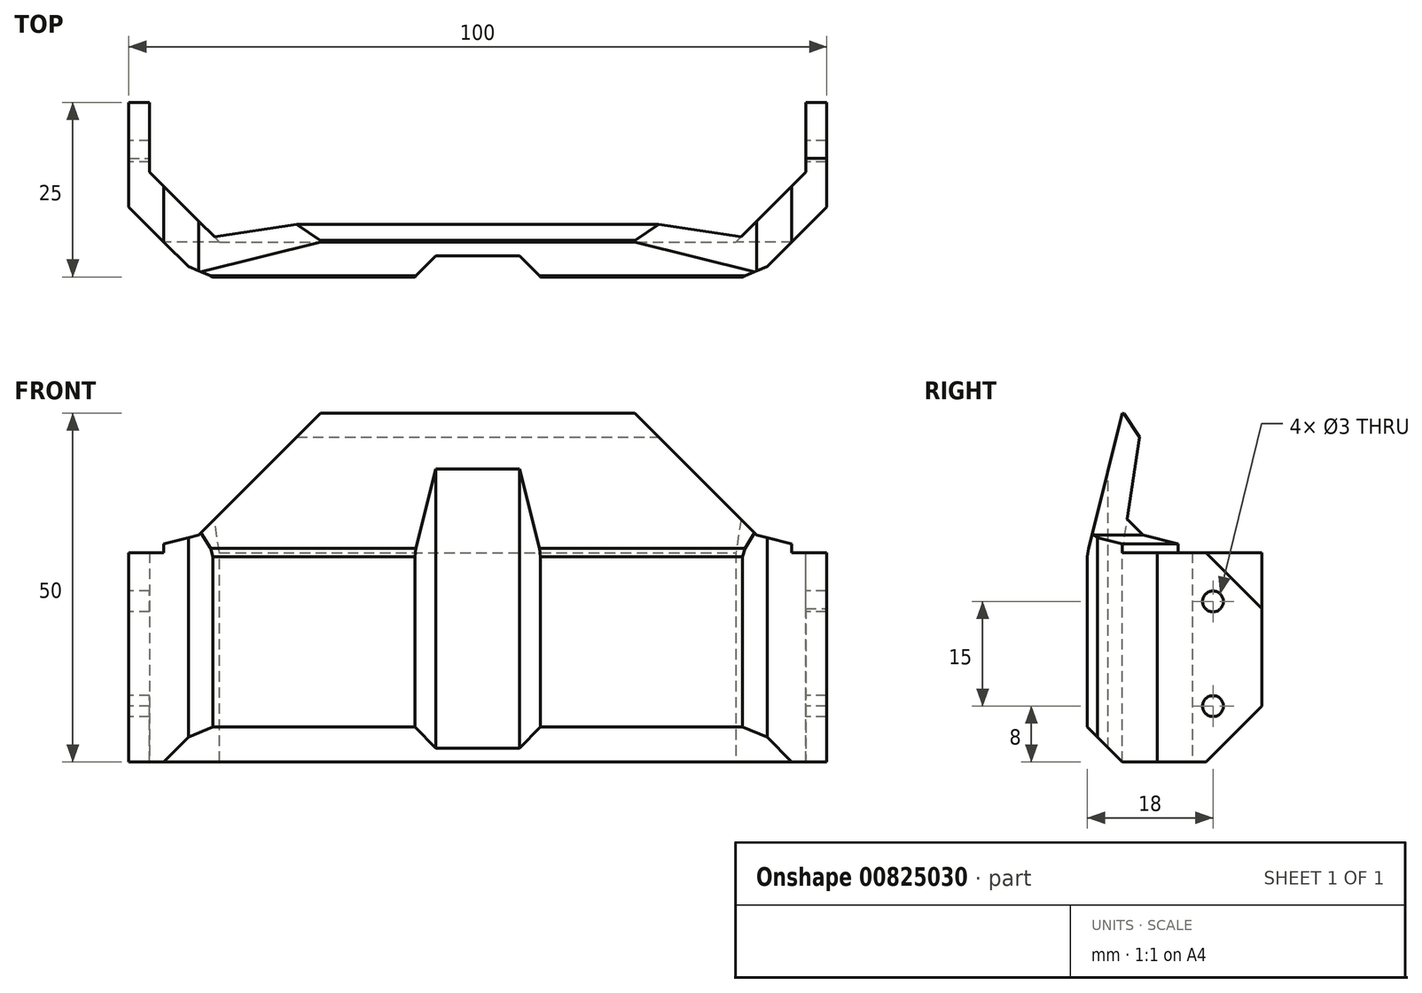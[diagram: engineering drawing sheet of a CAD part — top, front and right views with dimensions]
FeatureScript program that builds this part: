
annotation { "Feature Type Name" : "Feature", "Feature Type Description" : "" }
export const myFeature = defineFeature(function(context is Context, id is Id, definition is map)
    precondition{}
    {
        {
            var Q0;
            Q0=qCreatedBy(makeId("Top.planeOp"),FACE);
            var sketch = newSketch(context, id + "F0", { "sketchPlane" : qUnion([Q0])});
            skLineSegment(sketch, "E0.bottom", {"start": v(-50, 20) * mm, "end": v(50, 20) * mm});
            skLineSegment(sketch, "E0.top", {"start": v(-50, -5) * mm, "end": v(50, -5) * mm});
            skLineSegment(sketch, "E0.left", {"start": v(-50, 20) * mm, "end": v(-50, -5) * mm});
            skLineSegment(sketch, "E0.right", {"start": v(50, 20) * mm, "end": v(50, -5) * mm});
            skLineSegment(sketch, "E1.bottom", {"start": v(-47, 20) * mm, "end": v(47, 20) * mm});
            skLineSegment(sketch, "E1.top", {"start": v(-47, 0) * mm, "end": v(47, 0) * mm});
            skLineSegment(sketch, "E1.left", {"start": v(-47, 20) * mm, "end": v(-47, 0) * mm});
            skLineSegment(sketch, "E1.right", {"start": v(47, 20) * mm, "end": v(47, 0) * mm});
            skSolve(sketch);
        }
        {
            var Q0;
            Q0=makeQuery(id+"F0.imprint","IMPRINT",FACE,{"disambiguationData":[TD([[makeQuery(id+"F0.imprint","IMPRINT",EDGE,{"derivedFrom":sQuery(id+"F0.wireOp",EDGE,"E0.top")}),1.0]])]});
            extrude(context, id + "F1", {"entities" : qUnion([Q0]), "depth" : 30 * mm, "offsetDistance" : 25 * mm});
        }
        {
            var Q0;
            Q0=makeQuery(id+"F1.opExtrude","SWEPT_EDGE",EDGE,{"disambiguationData":[OSD([sQuery(id+"F0.wireOp",EDGE,"E1.top"),sQuery(id+"F0.wireOp",EDGE,"E1.left")])]});
            var Q1;
            Q1=makeQuery(id+"F1.opExtrude","SWEPT_EDGE",EDGE,{"disambiguationData":[OSD([sQuery(id+"F0.wireOp",EDGE,"E1.top"),sQuery(id+"F0.wireOp",EDGE,"E1.right")])]});
            var Q2;
            Q2=makeQuery(id+"F1.opExtrude","SWEPT_EDGE",EDGE,{"disambiguationData":[OSD([sQuery(id+"F0.wireOp",EDGE,"E0.top"),sQuery(id+"F0.wireOp",EDGE,"E0.left")])]});
            var Q3;
            Q3=makeQuery(id+"F1.opExtrude","SWEPT_EDGE",EDGE,{"disambiguationData":[OSD([sQuery(id+"F0.wireOp",EDGE,"E0.top"),sQuery(id+"F0.wireOp",EDGE,"E0.right")])]});
            chamfer(context, id + "F2", {"entities" : qUnion([Q0, Q1, Q2, Q3]), "width" : 10 * mm, "tangentPropagation" : true});
        }
        {
            var Q0;
            Q0=qCreatedBy(makeId("Right.planeOp"),FACE);
            var sketch = newSketch(context, id + "F3", { "sketchPlane" : qUnion([Q0])});
            skLineSegment(sketch, "E2.0.0", {"start": v(5, 30) * mm, "end": v(-5, 30) * mm});
            skLineSegment(sketch, "E2.0.1", {"start": v(5, 30) * mm, "end": v(5, 0) * mm});
            skLineSegment(sketch, "E2.0.2", {"start": v(-5, 0) * mm, "end": v(5, 0) * mm});
            skLineSegment(sketch, "E2.0.3", {"start": v(-5, 0) * mm, "end": v(-5, 30) * mm});
            skLineSegment(sketch, "E3", {"start": v(-5, 30) * mm, "end": v(0, 50) * mm});
            skLineSegment(sketch, "E4", {"start": v(0, 50) * mm, "end": v(2.91, 49.27) * mm});
            skLineSegment(sketch, "E5", {"start": v(2.91, 49.27) * mm, "end": v(0, 30) * mm});
            skSolve(sketch);
        }
        {
            var Q0;
            {var subQ0=sQuery(id+"F3.wireOp",EDGE,"E3");Q0=makeQuery(id+"F3.imprint","IMPRINT",FACE,{"disambiguationData":[TD([[makeQuery(id+"F3.imprint","IMPRINT",EDGE,{"derivedFrom":subQ0}),-1.0]])]});}
            extrude(context, id + "F4", {"entities" : qUnion([Q0]), "operationType" : NewBodyOperationType.ADD, "endBound" : BoundingType.SYMMETRIC, "depth" : 100 * mm, "offsetDistance" : 25 * mm});
        }
        {
            var Q0;
            {var subQ0=sQuery(id+"F0.wireOp",EDGE,"E1.right");var subQ1=sQuery(id+"F0.wireOp",EDGE,"E1.top");var subQ2=sQuery(id+"F0.wireOp",EDGE,"E0.right");var subQ3=sQuery(id+"F0.wireOp",EDGE,"E0.bottom");var subQ4=sQuery(id+"F0.wireOp",EDGE,"E0.top");Q0=makeQuery(id+"F4.boolean.opBoolean","SPLIT",FACE,{"disambiguationData":[TD([makeQuery(id+"F1.opExtrude","SWEPT_FACE",FACE,{"disambiguationData":[OSD([subQ2])]})])],"derivedFrom":makeQuery(id+"F1.opExtrude","CAP_FACE",FACE,{"disambiguationData":[OSD([subQ3,subQ4,sQuery(id+"F0.wireOp",EDGE,"E0.left"),subQ2,subQ1,sQuery(id+"F0.wireOp",EDGE,"E1.left"),subQ0])],"isStart":false})});}
            var Q1;
            {var subQ0=sQuery(id+"F0.wireOp",EDGE,"E1.left");var subQ1=sQuery(id+"F0.wireOp",EDGE,"E1.top");var subQ2=sQuery(id+"F0.wireOp",EDGE,"E0.left");var subQ3=sQuery(id+"F0.wireOp",EDGE,"E0.bottom");var subQ4=sQuery(id+"F0.wireOp",EDGE,"E0.top");Q1=makeQuery(id+"F4.boolean.opBoolean","SPLIT",FACE,{"disambiguationData":[TD([makeQuery(id+"F1.opExtrude","SWEPT_FACE",FACE,{"disambiguationData":[OSD([subQ2])]})])],"derivedFrom":makeQuery(id+"F1.opExtrude","CAP_FACE",FACE,{"disambiguationData":[OSD([subQ3,subQ4,subQ2,sQuery(id+"F0.wireOp",EDGE,"E0.right"),subQ1,subQ0,sQuery(id+"F0.wireOp",EDGE,"E1.right")])],"isStart":false})});}
            extrude(context, id + "F5", {"entities" : qUnion([Q0, Q1]), "operationType" : NewBodyOperationType.ADD, "depth" : 20 * mm, "offsetDistance" : 25 * mm});
        }
        {
            var Q0;
            {var subQ2=sQuery(id+"F3.wireOp",EDGE,"E2.0.0");var subQ3=sQuery(id+"F0.wireOp",EDGE,"E0.top");var subQ4=sQuery(id+"F0.wireOp",EDGE,"E0.right");Q0=makeQuery(id+"F4.boolean.opBoolean","SPLIT",FACE,{"disambiguationData":[TD([makeQuery(id+"F2.opChamfer","BLEND_FACE",FACE,{"disambiguationData":[OSD([subQ3,subQ4])]})])],"derivedFrom":makeQuery(id+"F4.opExtrude","SWEPT_FACE",FACE,{"disambiguationData":[OSD([subQ2])]})});}
            var Q1;
            {var subQ2=sQuery(id+"F3.wireOp",EDGE,"E2.0.0");var subQ3=sQuery(id+"F0.wireOp",EDGE,"E0.left");var subQ4=sQuery(id+"F0.wireOp",EDGE,"E0.top");Q1=makeQuery(id+"F4.boolean.opBoolean","SPLIT",FACE,{"disambiguationData":[TD([makeQuery(id+"F2.opChamfer","BLEND_FACE",FACE,{"disambiguationData":[OSD([subQ4,subQ3])]})])],"derivedFrom":makeQuery(id+"F4.opExtrude","SWEPT_FACE",FACE,{"disambiguationData":[OSD([subQ2])]})});}
            extrude(context, id + "F6", {"entities" : qUnion([Q0, Q1]), "operationType" : NewBodyOperationType.REMOVE, "oppositeDirection" : true, "depth" : 25 * mm, "offsetDistance" : 25 * mm});
        }
        {
            var Q0;
            Q0=makeQuery(id+"F1.opExtrude","SWEPT_FACE",FACE,{"disambiguationData":[OSD([sQuery(id+"F0.wireOp",EDGE,"E0.top")])]});
            var sketch = newSketch(context, id + "F7", { "sketchPlane" : qUnion([Q0])});
            skLineSegment(sketch, "E6.0.0", {"start": v(47.91, 49.27) * mm, "end": v(45, 30) * mm});
            skLineSegment(sketch, "E6.0.1", {"start": v(45, 30) * mm, "end": v(45, 50) * mm});
            skLineSegment(sketch, "E6.0.2", {"start": v(45, 50) * mm, "end": v(40, 30) * mm});
            skLineSegment(sketch, "E6.0.3", {"start": v(40, 30) * mm, "end": v(40, 0) * mm});
            skLineSegment(sketch, "E6.0.4", {"start": v(40, 0) * mm, "end": v(50, 0) * mm});
            skLineSegment(sketch, "E6.0.5", {"start": v(50, 0) * mm, "end": v(50, 50) * mm});
            skLineSegment(sketch, "E6.0.6", {"start": v(50, 50) * mm, "end": v(45, 50) * mm});
            skLineSegment(sketch, "E6.0.7", {"start": v(45, 50) * mm, "end": v(47.91, 49.27) * mm});
            skLineSegment(sketch, "E7", {"start": v(50, 30) * mm, "end": v(45, 30) * mm});
            skLineSegment(sketch, "E8.0.0", {"start": v(40, 30) * mm, "end": v(45, 50) * mm});
            skLineSegment(sketch, "E8.0.1", {"start": v(45, 50) * mm, "end": v(37, 50) * mm});
            skLineSegment(sketch, "E8.0.2", {"start": v(37, 50) * mm, "end": v(-37, 50) * mm});
            skLineSegment(sketch, "E8.0.3", {"start": v(-37, 50) * mm, "end": v(-45, 50) * mm});
            skLineSegment(sketch, "E8.0.4", {"start": v(-45, 50) * mm, "end": v(-40, 30) * mm});
            skLineSegment(sketch, "E8.0.5", {"start": v(-40, 30) * mm, "end": v(40, 30) * mm});
            skLineSegment(sketch, "E9", {"start": v(50, 30) * mm, "end": v(40, 32.5) * mm});
            skLineSegment(sketch, "E10", {"start": v(40, 32.5) * mm, "end": v(22.5, 50) * mm});
            skSolve(sketch);
        }
        {
            var Q0;
            {var subQ1=sQuery(id+"F7.wireOp",EDGE,"E8.0.1");Q0=makeQuery(id+"F7.imprint","IMPRINT",FACE,{"disambiguationData":[TD([[makeQuery(id+"F7.imprint","IMPRINT",EDGE,{"derivedFrom":subQ1}),1.0]])]});}
            var Q1;
            {var subQ1=sQuery(id+"F7.wireOp",EDGE,"E6.0.1");var subQ3=sQuery(id+"F7.wireOp",EDGE,"E9");var subQ4=makeQuery(id+"F7.imprint","INTERSECT",VERTEX,{"derivedFrom":[subQ1,subQ3]});Q1=makeQuery(id+"F7.imprint","IMPRINT",FACE,{"disambiguationData":[TD([[makeQuery(id+"F7.imprint","IMPRINT",EDGE,{"disambiguationData":[TD([[subQ4,-1.0]])],"derivedFrom":subQ3}),-1.0]])]});}
            var Q2;
            {var subQ1=sQuery(id+"F7.wireOp",EDGE,"E6.0.6");Q2=makeQuery(id+"F7.imprint","IMPRINT",FACE,{"disambiguationData":[TD([[makeQuery(id+"F7.imprint","IMPRINT",EDGE,{"derivedFrom":subQ1}),1.0]])]});}
            extrude(context, id + "F8", {"entities" : qUnion([Q0, Q1, Q2]), "operationType" : NewBodyOperationType.REMOVE, "endBound" : BoundingType.THROUGH_ALL, "oppositeDirection" : true, "depth" : 25 * mm, "offsetDistance" : 25 * mm});
        }
        {
            var Q0;
            {var subQ0=sQuery(id+"F3.wireOp",EDGE,"E5");var subQ1=sQuery(id+"F3.wireOp",EDGE,"E2.0.0");var subQ2=makeQuery(id+"F4.opExtrude","SWEPT_FACE",FACE,{"disambiguationData":[OSD([subQ1])]});var subQ3=sQuery(id+"F0.wireOp",EDGE,"E0.right");var subQ4=sQuery(id+"F0.wireOp",EDGE,"E0.top");var subQ5=makeQuery(id+"F4.opExtrude","SWEPT_FACE",FACE,{"disambiguationData":[OSD([subQ0])]});Q0=makeQuery(id+"F6.boolean.opBoolean","COPY",FACE,{"derivedFrom":makeQuery(id+"F6.opExtrude","SWEPT_FACE",FACE,{"disambiguationData":[OSD([subQ1,subQ0]),TDD([makeQuery(id+"F4.boolean.opBoolean","SPLIT",EDGE,{"disambiguationData":[topologyDisambiguationEdgeConnected([subQ2,subQ5]),TD([makeQuery(id+"F2.opChamfer","BLEND_FACE",FACE,{"disambiguationData":[OSD([subQ4,subQ3])]})])],"derivedFrom":makeQuery(id+"F4.opExtrude","SWEPT_EDGE",EDGE,{"disambiguationData":[OSD([subQ1,subQ0])]})})])]})});}
            extrude(context, id + "F9", {"entities" : qUnion([Q0]), "operationType" : NewBodyOperationType.REMOVE, "oppositeDirection" : true, "depth" : 25 * mm, "offsetDistance" : 25 * mm});
        }
        {
            var Q0;
            Q0=makeQuery(id+"F1.opExtrude","SWEPT_BODY",BODY,{"disambiguationData":[OSD([sQuery(id+"F0.wireOp",EDGE,"E0.bottom"),sQuery(id+"F0.wireOp",EDGE,"E0.top"),sQuery(id+"F0.wireOp",EDGE,"E0.left"),sQuery(id+"F0.wireOp",EDGE,"E0.right"),sQuery(id+"F0.wireOp",EDGE,"E1.top"),sQuery(id+"F0.wireOp",EDGE,"E1.left"),sQuery(id+"F0.wireOp",EDGE,"E1.right")])]});
            var Q1;
            Q1=qCreatedBy(makeId("Right.planeOp"),FACE);
            mirror(context, id + "F10", {"operationType" : NewBodyOperationType.INTERSECT, "entities" : qUnion([Q0]), "mirrorPlane" : qUnion([Q1])});
        }
        {
            var Q0;
            Q0=makeQuery(id+"F1.opExtrude","CAP_FACE",FACE,{"disambiguationData":[OSD([sQuery(id+"F0.wireOp",EDGE,"E0.bottom"),sQuery(id+"F0.wireOp",EDGE,"E0.top"),sQuery(id+"F0.wireOp",EDGE,"E0.left"),sQuery(id+"F0.wireOp",EDGE,"E0.right"),sQuery(id+"F0.wireOp",EDGE,"E1.top"),sQuery(id+"F0.wireOp",EDGE,"E1.left"),sQuery(id+"F0.wireOp",EDGE,"E1.right")])],"isStart":true});
            var sketch = newSketch(context, id + "F11", { "sketchPlane" : qUnion([Q0])});
            skLineSegment(sketch, "E11.bottom", {"start": v(4, 5) * mm, "end": v(-4, 5) * mm});
            skLineSegment(sketch, "E11.top", {"start": v(4, 2) * mm, "end": v(-4, 2) * mm});
            skLineSegment(sketch, "E11.left", {"start": v(4, 5) * mm, "end": v(4, 2) * mm});
            skLineSegment(sketch, "E11.right", {"start": v(-4, 5) * mm, "end": v(-4, 2) * mm});
            skSolve(sketch);
        }
        {
            var Q0;
            Q0=makeQuery(id+"F11.imprint","IMPRINT",FACE,{"disambiguationData":[TD([[makeQuery(id+"F11.imprint","IMPRINT",EDGE,{"derivedFrom":sQuery(id+"F11.wireOp",EDGE,"E11.bottom")}),-1.0]])]});
            extrude(context, id + "F12", {"entities" : qUnion([Q0]), "operationType" : NewBodyOperationType.REMOVE, "endBound" : BoundingType.THROUGH_ALL, "oppositeDirection" : true, "depth" : 25 * mm, "offsetDistance" : 25 * mm});
        }
        {
            var Q0;
            Q0=makeQuery(id+"F12.boolean.opBoolean","COPY",EDGE,{"derivedFrom":makeQuery(id+"F12.opExtrude","SWEPT_EDGE",EDGE,{"disambiguationData":[OSD([sQuery(id+"F0.wireOp",EDGE,"E0.top"),sQuery(id+"F11.wireOp",EDGE,"E11.bottom"),sQuery(id+"F11.wireOp",EDGE,"E11.left")])]})});
            var Q1;
            {var subQ5=sQuery(id+"F0.wireOp",EDGE,"E0.top");Q1=makeQuery(id+"F12.boolean.opBoolean","SPLIT",FACE,{"disambiguationData":[TD([makeQuery(id+"F12.opExtrude","SWEPT_FACE",FACE,{"disambiguationData":[OSD([sQuery(id+"F11.wireOp",EDGE,"E11.right")])]})])],"derivedFrom":makeQuery(id+"F1.opExtrude","SWEPT_FACE",FACE,{"disambiguationData":[OSD([subQ5])]})});}
            chamfer(context, id + "F13", {"entities" : qUnion([Q0, Q1]), "width" : 5 * mm, "tangentPropagation" : true});
        }
        {
            var Q0;
            {var subQ5=sQuery(id+"F0.wireOp",EDGE,"E0.top");Q0=makeQuery(id+"F12.boolean.opBoolean","SPLIT",EDGE,{"disambiguationData":[TD([makeQuery(id+"F12.opExtrude","SWEPT_FACE",FACE,{"disambiguationData":[OSD([sQuery(id+"F11.wireOp",EDGE,"E11.left")])]})])],"derivedFrom":makeQuery(id+"F1.opExtrude","CAP_EDGE",EDGE,{"disambiguationData":[OSD([subQ5])],"isStart":true})});}
            chamfer(context, id + "F14", {"entities" : qUnion([Q0]), "width" : 5 * mm, "tangentPropagation" : true});
        }
        {
            var Q0;
            {var subQ0=sQuery(id+"F0.wireOp",EDGE,"E0.left");Q0=makeQuery(id+"F5.boolean.opBoolean","MERGE",FACE,{"derivedFrom":[makeQuery(id+"F1.opExtrude","SWEPT_FACE",FACE,{"disambiguationData":[OSD([subQ0])]}),makeQuery(id+"F5.opExtrude","SWEPT_FACE",FACE,{"disambiguationData":[OSD([subQ0])]})]});}
            var sketch = newSketch(context, id + "F15", { "sketchPlane" : qUnion([Q0])});
            skCircle(sketch, "E12", {"center": v(-13, 8) * mm, "radius": 1.5 * mm});
            skCircle(sketch, "E13", {"center": v(-13, 23) * mm, "radius": 1.5 * mm});
            skSolve(sketch);
        }
        {
            var Q0;
            Q0=makeQuery(id+"F15.imprint","IMPRINT",FACE,{"disambiguationData":[TD([[makeQuery(id+"F15.imprint","IMPRINT",EDGE,{"derivedFrom":sQuery(id+"F15.wireOp",EDGE,"E13")}),1.0]])]});
            var Q1;
            Q1=makeQuery(id+"F15.imprint","IMPRINT",FACE,{"disambiguationData":[TD([[makeQuery(id+"F15.imprint","IMPRINT",EDGE,{"derivedFrom":sQuery(id+"F15.wireOp",EDGE,"E12")}),1.0]])]});
            extrude(context, id + "F16", {"entities" : qUnion([Q0, Q1]), "operationType" : NewBodyOperationType.REMOVE, "endBound" : BoundingType.THROUGH_ALL, "oppositeDirection" : true, "depth" : 25 * mm, "offsetDistance" : 25 * mm});
        }
        {
            var Q0;
            Q0=makeQuery(id+"F1.opExtrude","SWEPT_BODY",BODY,{"disambiguationData":[OSD([sQuery(id+"F0.wireOp",EDGE,"E0.bottom"),sQuery(id+"F0.wireOp",EDGE,"E0.top"),sQuery(id+"F0.wireOp",EDGE,"E0.left"),sQuery(id+"F0.wireOp",EDGE,"E0.right"),sQuery(id+"F0.wireOp",EDGE,"E1.top"),sQuery(id+"F0.wireOp",EDGE,"E1.left"),sQuery(id+"F0.wireOp",EDGE,"E1.right")])]});
            var Q1;
            Q1=qCreatedBy(makeId("Right.planeOp"),FACE);
            mirror(context, id + "F17", {"operationType" : NewBodyOperationType.INTERSECT, "entities" : qUnion([Q0]), "mirrorPlane" : qUnion([Q1])});
        }
        {
            var Q0;
            {var subQ0=sQuery(id+"F0.wireOp",EDGE,"E0.bottom");Q0=makeQuery(id+"F1.opExtrude","CAP_EDGE",EDGE,{"disambiguationData":[OSD([subQ0]),TDD([makeQuery(id+"F0.imprint","IMPRINT",EDGE,{"disambiguationData":[TD([[makeQuery(id+"F0.imprint","INTERSECT",VERTEX,{"derivedFrom":[subQ0,sQuery(id+"F0.wireOp",EDGE,"E0.right")]}),1.0]])],"derivedFrom":subQ0})])],"isStart":true});}
            var Q1;
            {var subQ0=sQuery(id+"F0.wireOp",EDGE,"E0.bottom");Q1=makeQuery(id+"F1.opExtrude","CAP_EDGE",EDGE,{"disambiguationData":[OSD([subQ0]),TDD([makeQuery(id+"F0.imprint","IMPRINT",EDGE,{"disambiguationData":[TD([[makeQuery(id+"F0.imprint","INTERSECT",VERTEX,{"derivedFrom":[subQ0,sQuery(id+"F0.wireOp",EDGE,"E0.left")]}),-1.0]])],"derivedFrom":subQ0})])],"isStart":true});}
            var Q2;
            {var subQ1=sQuery(id+"F0.wireOp",EDGE,"E0.right");var subQ2=sQuery(id+"F0.wireOp",EDGE,"E0.bottom");var subQ4=makeQuery(id+"F0.imprint","IMPRINT",EDGE,{"disambiguationData":[TD([[makeQuery(id+"F0.imprint","INTERSECT",VERTEX,{"derivedFrom":[subQ2,subQ1]}),1.0]])],"derivedFrom":subQ2});Q2=makeQuery(id+"F10.boolean.opBoolean","COPY",EDGE,{"derivedFrom":makeQuery(id+"F10.boolean.toolComplement.opBoolean","COPY",EDGE,{"derivedFrom":makeQuery(id+"F10.opPattern","COPY",EDGE,{"derivedFrom":makeQuery(id+"F9.boolean.opBoolean","INTERSECT",EDGE,{"derivedFrom":[makeQuery(id+"F8.boolean.opBoolean","SPLIT",FACE,{"disambiguationData":[TD([makeQuery(id+"F1.opExtrude","SWEPT_FACE",FACE,{"disambiguationData":[OSD([subQ1])]})])],"derivedFrom":makeQuery(id+"F5.boolean.opBoolean","MERGE",FACE,{"derivedFrom":[makeQuery(id+"F1.opExtrude","SWEPT_FACE",FACE,{"disambiguationData":[OSD([subQ2]),TDD([subQ4])]}),makeQuery(id+"F5.opExtrude","SWEPT_FACE",FACE,{"disambiguationData":[OSD([subQ2]),TDD([makeQuery(id+"F1.opExtrude","CAP_EDGE",EDGE,{"disambiguationData":[OSD([subQ2]),TDD([subQ4])],"isStart":false})])]})]})}),makeQuery(id+"F9.opExtrude","SWEPT_FACE",FACE,{"disambiguationData":[OSD([sQuery(id+"F3.wireOp",EDGE,"E2.0.0"),sQuery(id+"F3.wireOp",EDGE,"E5")])]})]}),"instanceName":"1"})})});}
            var Q3;
            {var subQ1=sQuery(id+"F0.wireOp",EDGE,"E0.right");var subQ2=sQuery(id+"F0.wireOp",EDGE,"E0.bottom");var subQ4=makeQuery(id+"F0.imprint","IMPRINT",EDGE,{"disambiguationData":[TD([[makeQuery(id+"F0.imprint","INTERSECT",VERTEX,{"derivedFrom":[subQ2,subQ1]}),1.0]])],"derivedFrom":subQ2});Q3=makeQuery(id+"F9.boolean.opBoolean","INTERSECT",EDGE,{"derivedFrom":[makeQuery(id+"F8.boolean.opBoolean","SPLIT",FACE,{"disambiguationData":[TD([makeQuery(id+"F1.opExtrude","SWEPT_FACE",FACE,{"disambiguationData":[OSD([subQ1])]})])],"derivedFrom":makeQuery(id+"F5.boolean.opBoolean","MERGE",FACE,{"derivedFrom":[makeQuery(id+"F1.opExtrude","SWEPT_FACE",FACE,{"disambiguationData":[OSD([subQ2]),TDD([subQ4])]}),makeQuery(id+"F5.opExtrude","SWEPT_FACE",FACE,{"disambiguationData":[OSD([subQ2]),TDD([makeQuery(id+"F1.opExtrude","CAP_EDGE",EDGE,{"disambiguationData":[OSD([subQ2]),TDD([subQ4])],"isStart":false})])]})]})}),makeQuery(id+"F9.opExtrude","SWEPT_FACE",FACE,{"disambiguationData":[OSD([sQuery(id+"F3.wireOp",EDGE,"E2.0.0"),sQuery(id+"F3.wireOp",EDGE,"E5")])]})]});}
            chamfer(context, id + "F18", {"entities" : qUnion([Q0, Q1, Q2, Q3]), "width" : 8 * mm, "tangentPropagation" : true});
        }
        {
            var Q0;
            {var subQ0=sQuery(id+"F3.wireOp",EDGE,"E5");var subQ2=sQuery(id+"F0.wireOp",EDGE,"E1.top");var subQ3=sQuery(id+"F3.wireOp",EDGE,"E4");var subQ4=sQuery(id+"F0.wireOp",EDGE,"E1.left");Q0=makeQuery(id+"F5.boolean.opBoolean","SPLIT",EDGE,{"disambiguationData":[TD([makeQuery(id+"F2.opChamfer","BLEND_FACE",FACE,{"disambiguationData":[OSD([subQ2,subQ4])]})])],"derivedFrom":makeQuery(id+"F4.opExtrude","SWEPT_EDGE",EDGE,{"disambiguationData":[OSD([subQ3,subQ0])]})});}
            chamfer(context, id + "F19", {"entities" : qUnion([Q0]), "width" : 3 * mm, "tangentPropagation" : true});
        }
    });
